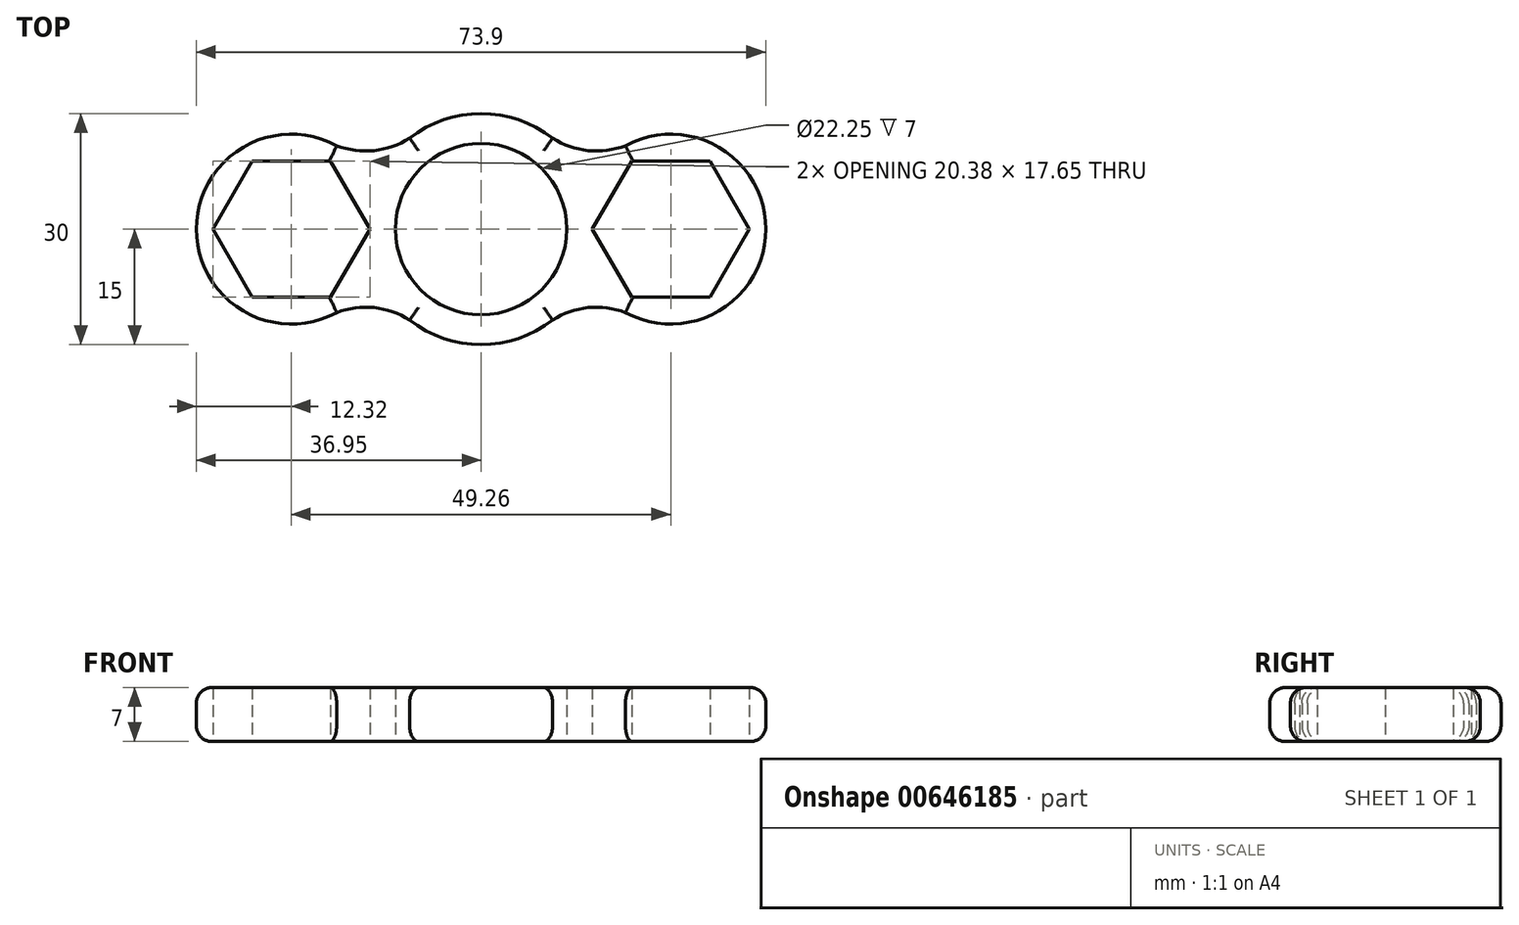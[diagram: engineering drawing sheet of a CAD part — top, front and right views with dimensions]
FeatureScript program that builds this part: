
annotation { "Feature Type Name" : "Feature", "Feature Type Description" : "" }
export const myFeature = defineFeature(function(context is Context, id is Id, definition is map)
    precondition{}
    {
        {
            var Q0;
            Q0=qCreatedBy(makeId("Top.planeOp"),FACE);
            var sketch = newSketch(context, id + "F0", { "sketchPlane" : qUnion([Q0])});
            skCircle(sketch, "E0", {"center": v(0, 0) * mm, "radius": 11.12 * mm});
            skArc(sketch, "E1", {"start": v(9.28, 11.79) * mm, "mid": v(0, 15) * mm, "end": v(-9.28, 11.79) * mm});
            skLineSegment(sketch, "E2", {"start": v(0, 0) * mm, "end": v(35, 0) * mm, "construction": true});
            skCircle(sketch, "E3.cCircle", {"center": v(24.63, 0) * mm, "radius": 8.82 * mm, "construction": true});
            skLineSegment(sketch, "E3.0", {"start": v(19.54, 8.82) * mm, "end": v(29.73, 8.82) * mm});
            skLineSegment(sketch, "E3.1", {"start": v(29.73, 8.82) * mm, "end": v(34.82, 0) * mm});
            skLineSegment(sketch, "E3.2", {"start": v(34.82, 0) * mm, "end": v(29.73, -8.82) * mm});
            skLineSegment(sketch, "E3.3", {"start": v(29.73, -8.82) * mm, "end": v(19.54, -8.82) * mm});
            skLineSegment(sketch, "E3.4", {"start": v(19.54, -8.82) * mm, "end": v(14.44, 0) * mm});
            skLineSegment(sketch, "E3.5", {"start": v(14.44, 0) * mm, "end": v(19.54, 8.82) * mm});
            skPoint(sketch, "E3.0.midPoint", {"position": v(24.63, 8.82) * mm});
            skArc(sketch, "E4", {"start": v(18.75, -10.83) * mm, "mid": v(36.95, 0) * mm, "end": v(18.75, 10.83) * mm});
            skArc(sketch, "E5", {"start": v(18.75, -10.83) * mm, "mid": v(13.9, -10.2) * mm, "end": v(9.28, -11.79) * mm});
            skArc(sketch, "E6.MirrorCS", {"start": v(18.75, 10.83) * mm, "mid": v(13.9, 10.2) * mm, "end": v(9.28, 11.79) * mm});
            skPoint(sketch, "E7.MirrorP", {"position": v(-24.63, 8.82) * mm});
            skLineSegment(sketch, "E8.MirrorCS", {"start": v(0, 0) * mm, "end": v(-35, 0) * mm, "construction": true});
            skArc(sketch, "E9.MirrorCS", {"start": v(-18.75, 10.83) * mm, "mid": v(-13.9, 10.2) * mm, "end": v(-9.28, 11.79) * mm});
            skCircle(sketch, "E10.MirrorC", {"center": v(-24.63, 0) * mm, "radius": 8.82 * mm, "construction": true});
            skLineSegment(sketch, "E11.MirrorCS", {"start": v(-19.54, 8.83) * mm, "end": v(-29.73, 8.83) * mm});
            skLineSegment(sketch, "E12.MirrorCS", {"start": v(-29.73, 8.82) * mm, "end": v(-34.82, 0) * mm});
            skLineSegment(sketch, "E13.MirrorCS", {"start": v(-34.82, 0) * mm, "end": v(-29.73, -8.82) * mm});
            skLineSegment(sketch, "E14.MirrorCS", {"start": v(-29.73, -8.83) * mm, "end": v(-19.54, -8.83) * mm});
            skLineSegment(sketch, "E15.MirrorCS", {"start": v(-19.54, -8.82) * mm, "end": v(-14.44, 0) * mm});
            skArc(sketch, "E16.MirrorCS", {"start": v(-18.75, -10.83) * mm, "mid": v(-36.95, 0) * mm, "end": v(-18.75, 10.83) * mm});
            skArc(sketch, "E17.MirrorCS", {"start": v(-18.75, -10.83) * mm, "mid": v(-13.9, -10.2) * mm, "end": v(-9.28, -11.79) * mm});
            skLineSegment(sketch, "E18.MirrorCS", {"start": v(-14.44, 0) * mm, "end": v(-19.54, 8.82) * mm});
            skArc(sketch, "E19.trimOffspring", {"start": v(-9.28, -11.79) * mm, "mid": v(0, -15) * mm, "end": v(9.28, -11.79) * mm});
            skPoint(sketch, "E20.orphan", {"position": v(-13.8, 5.88) * mm});
            skPoint(sketch, "E21.orphan", {"position": v(13.8, 5.88) * mm});
            skSolve(sketch);
        }
        {
            var Q0;
            Q0=makeQuery(id+"F0.imprint","IMPRINT",FACE,{"disambiguationData":[TD([[makeQuery(id+"F0.imprint","IMPRINT",EDGE,{"derivedFrom":sQuery(id+"F0.wireOp",EDGE,"E0")}),-1.0]])]});
            extrude(context, id + "F1", {"entities" : qUnion([Q0]), "depth" : 7 * mm, "offsetDistance" : 25 * mm});
        }
        {
            var Q0;
            Q0=makeQuery(id+"F1.opExtrude","CAP_EDGE",EDGE,{"disambiguationData":[OSD([sQuery(id+"F0.wireOp",EDGE,"E16.MirrorCS")])],"isStart":false});
            var Q1;
            Q1=makeQuery(id+"F1.opExtrude","CAP_EDGE",EDGE,{"disambiguationData":[OSD([sQuery(id+"F0.wireOp",EDGE,"E17.MirrorCS")])],"isStart":false});
            var Q2;
            Q2=makeQuery(id+"F1.opExtrude","CAP_EDGE",EDGE,{"disambiguationData":[OSD([sQuery(id+"F0.wireOp",EDGE,"E19.trimOffspring")])],"isStart":false});
            var Q3;
            Q3=makeQuery(id+"F1.opExtrude","CAP_EDGE",EDGE,{"disambiguationData":[OSD([sQuery(id+"F0.wireOp",EDGE,"E5")])],"isStart":false});
            var Q4;
            Q4=makeQuery(id+"F1.opExtrude","CAP_EDGE",EDGE,{"disambiguationData":[OSD([sQuery(id+"F0.wireOp",EDGE,"E4")])],"isStart":false});
            var Q5;
            Q5=makeQuery(id+"F1.opExtrude","CAP_EDGE",EDGE,{"disambiguationData":[OSD([sQuery(id+"F0.wireOp",EDGE,"E6.MirrorCS")])],"isStart":false});
            var Q6;
            Q6=makeQuery(id+"F1.opExtrude","CAP_EDGE",EDGE,{"disambiguationData":[OSD([sQuery(id+"F0.wireOp",EDGE,"E1")])],"isStart":false});
            var Q7;
            Q7=makeQuery(id+"F1.opExtrude","CAP_EDGE",EDGE,{"disambiguationData":[OSD([sQuery(id+"F0.wireOp",EDGE,"E9.MirrorCS")])],"isStart":false});
            fillet(context, id + "F2", {"entities" : qUnion([Q0, Q1, Q2, Q3, Q4, Q5, Q6, Q7]), "radius" : 2 * mm, "tangentPropagation" : true, "allowEdgeOverflow" : false});
        }
        {
            var Q0;
            Q0=makeQuery(id+"F1.opExtrude","CAP_EDGE",EDGE,{"disambiguationData":[OSD([sQuery(id+"F0.wireOp",EDGE,"E17.MirrorCS")])],"isStart":true});
            var Q1;
            Q1=makeQuery(id+"F1.opExtrude","CAP_EDGE",EDGE,{"disambiguationData":[OSD([sQuery(id+"F0.wireOp",EDGE,"E16.MirrorCS")])],"isStart":true});
            var Q2;
            Q2=makeQuery(id+"F1.opExtrude","CAP_EDGE",EDGE,{"disambiguationData":[OSD([sQuery(id+"F0.wireOp",EDGE,"E9.MirrorCS")])],"isStart":true});
            var Q3;
            Q3=makeQuery(id+"F1.opExtrude","CAP_EDGE",EDGE,{"disambiguationData":[OSD([sQuery(id+"F0.wireOp",EDGE,"E1")])],"isStart":true});
            var Q4;
            Q4=makeQuery(id+"F1.opExtrude","CAP_EDGE",EDGE,{"disambiguationData":[OSD([sQuery(id+"F0.wireOp",EDGE,"E6.MirrorCS")])],"isStart":true});
            var Q5;
            Q5=makeQuery(id+"F1.opExtrude","CAP_EDGE",EDGE,{"disambiguationData":[OSD([sQuery(id+"F0.wireOp",EDGE,"E4")])],"isStart":true});
            var Q6;
            Q6=makeQuery(id+"F1.opExtrude","CAP_EDGE",EDGE,{"disambiguationData":[OSD([sQuery(id+"F0.wireOp",EDGE,"E5")])],"isStart":true});
            var Q7;
            Q7=makeQuery(id+"F1.opExtrude","CAP_EDGE",EDGE,{"disambiguationData":[OSD([sQuery(id+"F0.wireOp",EDGE,"E19.trimOffspring")])],"isStart":true});
            fillet(context, id + "F3", {"entities" : qUnion([Q0, Q1, Q2, Q3, Q4, Q5, Q6, Q7]), "radius" : 2 * mm, "tangentPropagation" : true, "allowEdgeOverflow" : false});
        }
    });
